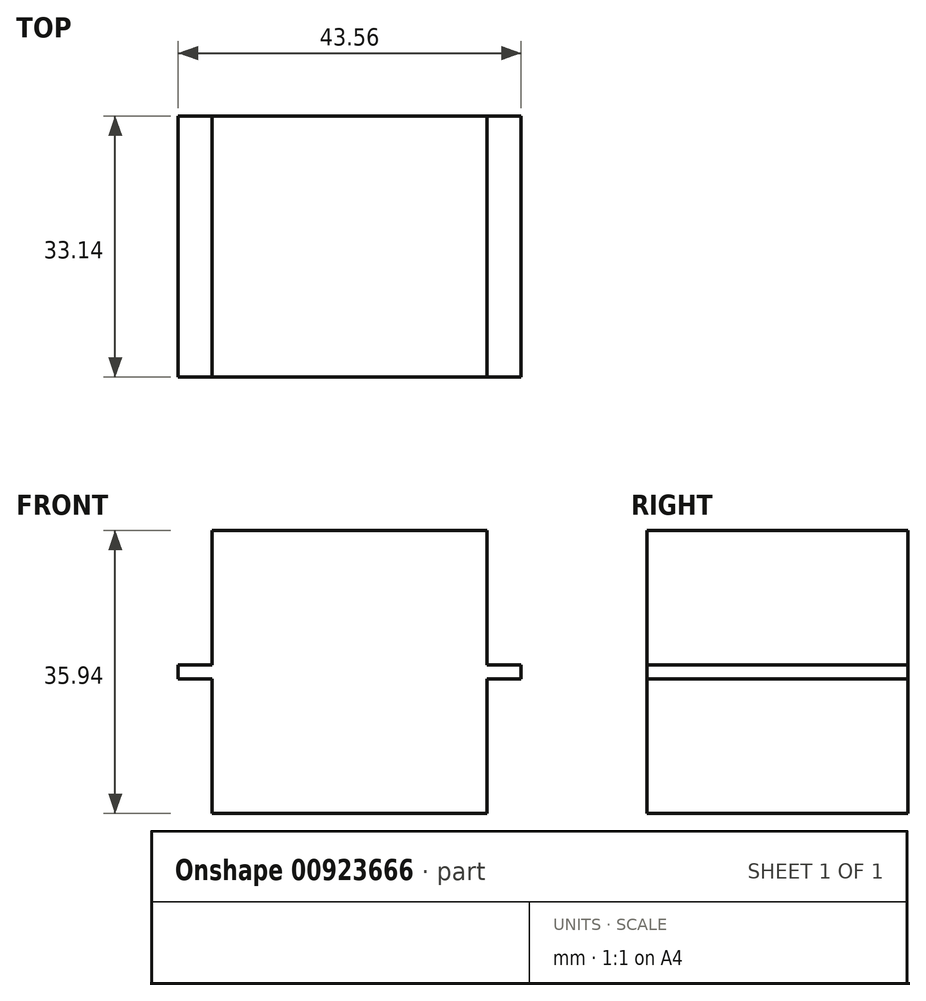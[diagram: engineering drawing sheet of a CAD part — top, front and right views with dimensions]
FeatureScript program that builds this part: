
annotation { "Feature Type Name" : "Feature", "Feature Type Description" : "" }
export const myFeature = defineFeature(function(context is Context, id is Id, definition is map)
    precondition{}
    {
        {
            var Q0;
            Q0=qCreatedBy(makeId("Top.planeOp"),FACE);
            var sketch = newSketch(context, id + "F0", { "sketchPlane" : qUnion([Q0])});
            skLineSegment(sketch, "E0.bottom", {"start": v(21.78, 16.57) * mm, "end": v(-21.78, 16.57) * mm});
            skLineSegment(sketch, "E0.top", {"start": v(21.78, -16.57) * mm, "end": v(-21.78, -16.57) * mm});
            skLineSegment(sketch, "E0.left", {"start": v(21.78, 16.57) * mm, "end": v(21.78, -16.57) * mm});
            skLineSegment(sketch, "E0.right", {"start": v(-21.78, 16.57) * mm, "end": v(-21.78, -16.57) * mm});
            skPoint(sketch, "E0.middle", {"position": v(0, 0) * mm});
            skSolve(sketch);
        }
        {
            var Q0;
            Q0 = qSketchRegion(id + "F0", true);
            extrude(context, id + "F1", {"entities" : qUnion([Q0]), "depth" : 35.94 * mm, "offsetDistance" : 25.4 * mm});
        }
        {
            var Q0;
            Q0=makeQuery(id+"F1.opExtrude","SWEPT_FACE",FACE,{"disambiguationData":[OSD([sQuery(id+"F0.wireOp",EDGE,"E0.top")])]});
            var sketch = newSketch(context, id + "F2", { "sketchPlane" : qUnion([Q0])});
            skLineSegment(sketch, "E1.0", {"start": v(-21.78, 35.94) * mm, "end": v(-21.78, 18.86) * mm});
            skLineSegment(sketch, "E2.0", {"start": v(21.78, 35.94) * mm, "end": v(17.46, 35.94) * mm});
            skLineSegment(sketch, "E3.0", {"start": v(21.78, 35.94) * mm, "end": v(21.78, 18.86) * mm});
            skLineSegment(sketch, "E4.0", {"start": v(21.78, 0) * mm, "end": v(17.46, 0) * mm});
            skLineSegment(sketch, "E5", {"start": v(0, 0) * mm, "end": v(0, 55.46) * mm, "construction": true});
            skLineSegment(sketch, "E6", {"start": v(17.46, 35.94) * mm, "end": v(17.46, 18.86) * mm});
            skLineSegment(sketch, "E7", {"start": v(17.46, 18.86) * mm, "end": v(21.78, 18.86) * mm});
            skLineSegment(sketch, "E8", {"start": v(-21.78, 17.97) * mm, "end": v(21.78, 17.97) * mm, "construction": true});
            skLineSegment(sketch, "E9.MirrorCS", {"start": v(17.46, 17.08) * mm, "end": v(21.78, 17.08) * mm});
            skLineSegment(sketch, "E10.MirrorCS", {"start": v(17.46, 0) * mm, "end": v(17.46, 17.08) * mm});
            skLineSegment(sketch, "E11.MirrorCS", {"start": v(-17.46, 35.94) * mm, "end": v(-17.46, 18.86) * mm});
            skLineSegment(sketch, "E12.MirrorCS", {"start": v(-17.46, 18.86) * mm, "end": v(-21.78, 18.86) * mm});
            skLineSegment(sketch, "E13.MirrorCS", {"start": v(-17.46, 17.08) * mm, "end": v(-21.78, 17.08) * mm});
            skLineSegment(sketch, "E14.MirrorCS", {"start": v(-17.46, 0) * mm, "end": v(-17.46, 17.08) * mm});
            skLineSegment(sketch, "E15.trimOffspring", {"start": v(-17.46, 35.94) * mm, "end": v(-21.78, 35.94) * mm});
            skLineSegment(sketch, "E16.trimOffspring", {"start": v(-17.46, 0) * mm, "end": v(-21.78, 0) * mm});
            skLineSegment(sketch, "E17.trimOffspring", {"start": v(21.78, 17.08) * mm, "end": v(21.78, 0) * mm});
            skLineSegment(sketch, "E18.trimOffspring", {"start": v(-21.78, 17.08) * mm, "end": v(-21.78, 0) * mm});
            skSolve(sketch);
        }
        {
            var Q0;
            Q0 = qSketchRegion(id + "F2", true);
            extrude(context, id + "F3", {"entities" : qUnion([Q0]), "operationType" : NewBodyOperationType.REMOVE, "endBound" : BoundingType.THROUGH_ALL, "oppositeDirection" : true, "depth" : 25.4 * mm, "offsetDistance" : 25.4 * mm});
        }
    });
